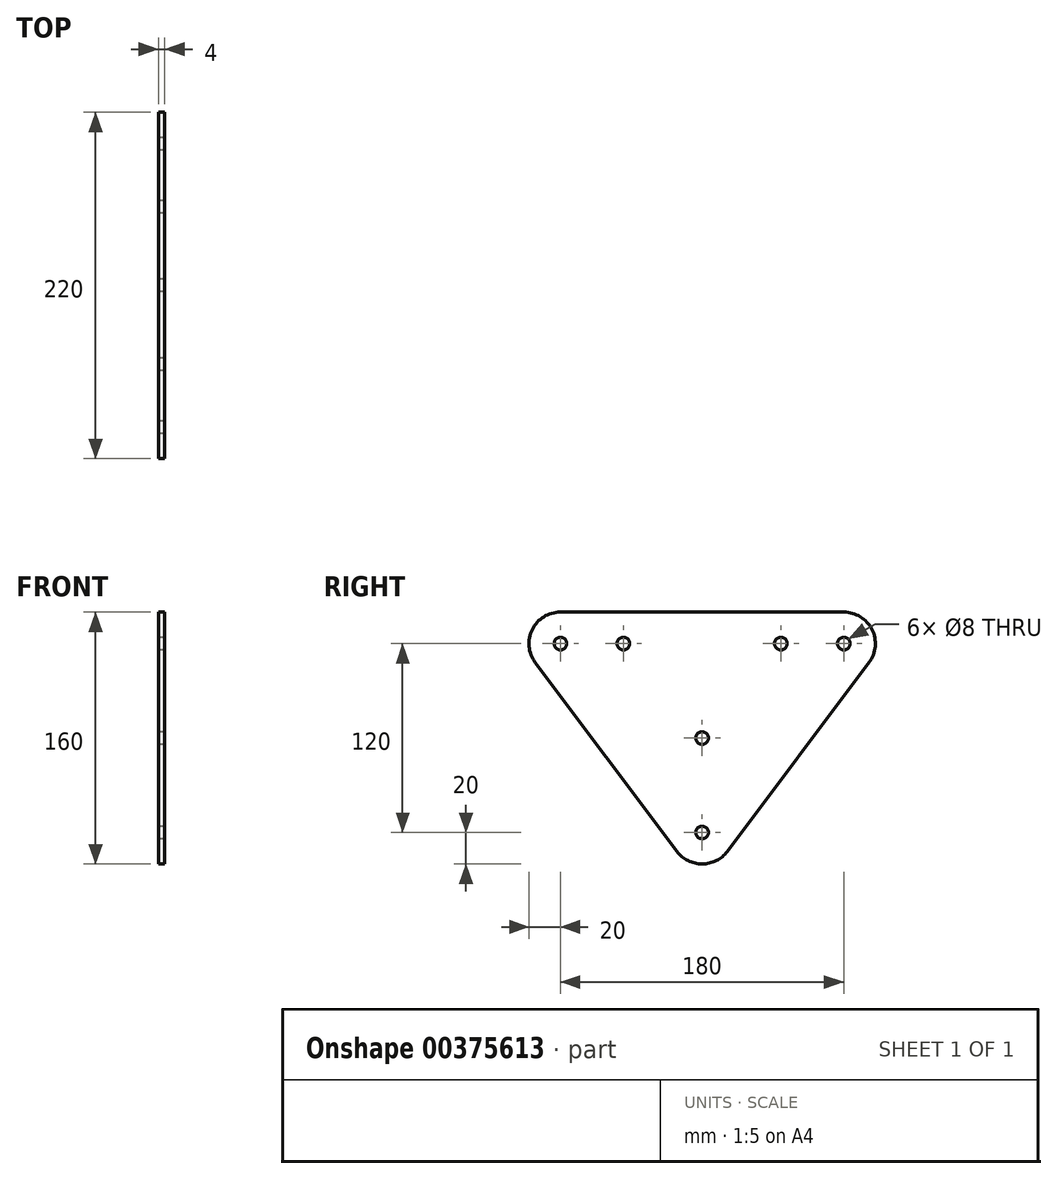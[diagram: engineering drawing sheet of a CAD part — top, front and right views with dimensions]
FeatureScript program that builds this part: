
annotation { "Feature Type Name" : "Feature", "Feature Type Description" : "" }
export const myFeature = defineFeature(function(context is Context, id is Id, definition is map)
    precondition{}
    {
        {
            var Q0;
            Q0=qCreatedBy(makeId("Right.planeOp"),FACE);
            var sketch = newSketch(context, id + "F0", { "sketchPlane" : qUnion([Q0])});
            skLineSegment(sketch, "E0.bottom", {"start": v(50, 40) * mm, "end": v(-50, 40) * mm, "construction": true});
            skLineSegment(sketch, "E0.top", {"start": v(50, -40) * mm, "end": v(-50, -40) * mm, "construction": true});
            skLineSegment(sketch, "E0.left", {"start": v(50, 40) * mm, "end": v(50, -40) * mm, "construction": true});
            skLineSegment(sketch, "E0.right", {"start": v(-50, 40) * mm, "end": v(-50, -40) * mm, "construction": true});
            skPoint(sketch, "E0.middle", {"position": v(0, 0) * mm});
            skCircle(sketch, "E1", {"center": v(-50, 60) * mm, "radius": 20 * mm, "construction": true});
            skCircle(sketch, "E2", {"center": v(50, 60) * mm, "radius": 20 * mm, "construction": true});
            skArc(sketch, "E3", {"start": v(-16, -72) * mm, "mid": v(0, -80) * mm, "end": v(16, -72) * mm});
            skPoint(sketch, "E3.centerSnap0", {"position": v(0, -40) * mm});
            skArc(sketch, "E4", {"start": v(106, 48) * mm, "mid": v(107.89, 68.94) * mm, "end": v(90, 80) * mm});
            skArc(sketch, "E5", {"start": v(-90, 80) * mm, "mid": v(-107.89, 68.94) * mm, "end": v(-106, 48) * mm});
            skLineSegment(sketch, "E6", {"start": v(-90, 80) * mm, "end": v(90, 80) * mm});
            skLineSegment(sketch, "E7", {"start": v(-106, 48) * mm, "end": v(-16, -72) * mm});
            skLineSegment(sketch, "E8", {"start": v(106, 48) * mm, "end": v(16, -72) * mm});
            skCircle(sketch, "E9", {"center": v(0, -60) * mm, "radius": 4 * mm});
            skCircle(sketch, "E10", {"center": v(90, 60) * mm, "radius": 4 * mm});
            skCircle(sketch, "E11", {"center": v(50, 60) * mm, "radius": 4 * mm});
            skCircle(sketch, "E12", {"center": v(-50, 60) * mm, "radius": 4 * mm});
            skCircle(sketch, "E13", {"center": v(-90, 60) * mm, "radius": 4 * mm});
            skCircle(sketch, "E14", {"center": v(0, 0) * mm, "radius": 4 * mm});
            skSolve(sketch);
        }
        {
            var Q0;
            Q0 = qSketchRegion(id + "F0", true);
            extrude(context, id + "F1", {"entities" : qUnion([Q0]), "depth" : 4 * mm});
        }
    });
